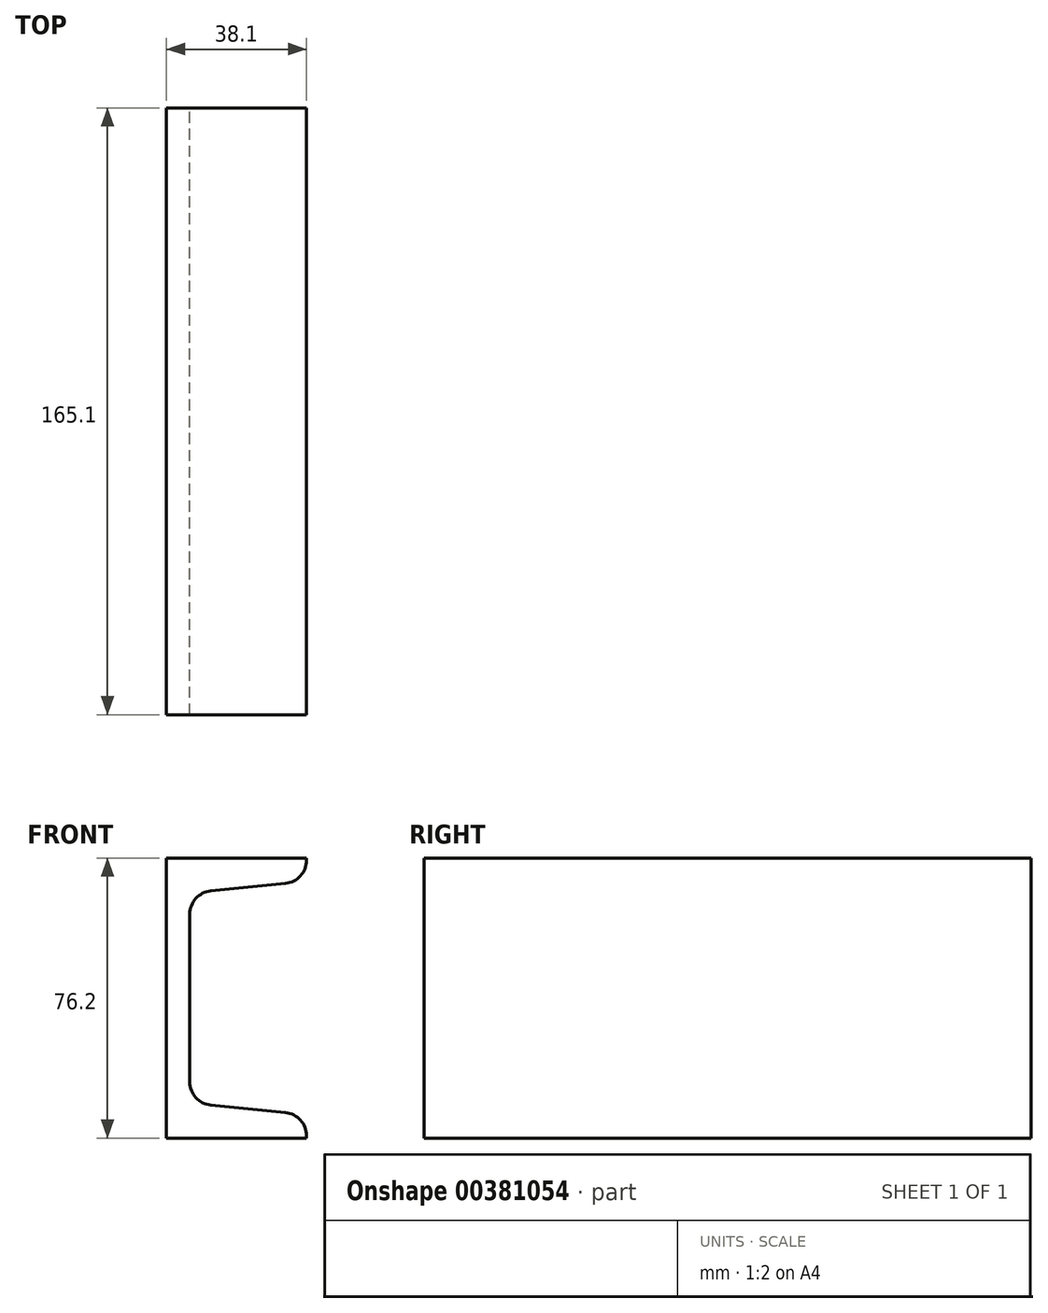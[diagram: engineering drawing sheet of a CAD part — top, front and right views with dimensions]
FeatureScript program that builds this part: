
annotation { "Feature Type Name" : "Feature", "Feature Type Description" : "" }
export const myFeature = defineFeature(function(context is Context, id is Id, definition is map)
    precondition{}
    {
        {
            var Q0;
            Q0=qCreatedBy(makeId("Front.planeOp"),FACE);
            var sketch = newSketch(context, id + "F0", { "sketchPlane" : qUnion([Q0])});
            skLineSegment(sketch, "E0", {"start": v(-3.27, 34.67) * mm, "end": v(-3.27, -41.53) * mm});
            skLineSegment(sketch, "E1", {"start": v(-3.27, 34.67) * mm, "end": v(34.83, 34.67) * mm});
            skLineSegment(sketch, "E2", {"start": v(34.83, -41.53) * mm, "end": v(34.83, -40.92) * mm});
            skLineSegment(sketch, "E3", {"start": v(29.11, -34.6) * mm, "end": v(8.8, -32.57) * mm});
            skLineSegment(sketch, "E4", {"start": v(3.08, -26.25) * mm, "end": v(3.08, 19.4) * mm});
            skLineSegment(sketch, "E5", {"start": v(8.8, 25.72) * mm, "end": v(29.11, 27.75) * mm});
            skLineSegment(sketch, "E6", {"start": v(34.83, 34.67) * mm, "end": v(34.83, 34.07) * mm});
            skLineSegment(sketch, "E7", {"start": v(-3.27, -41.53) * mm, "end": v(34.83, -41.53) * mm});
            skPoint(sketch, "E8.visualSharp", {"position": v(34.83, -35.18) * mm});
            skArc(sketch, "E8.filletArc", {"start": v(34.83, -40.92) * mm, "mid": v(33.19, -36.66) * mm, "end": v(29.11, -34.6) * mm});
            skPoint(sketch, "E9.visualSharp", {"position": v(34.83, 28.32) * mm});
            skArc(sketch, "E9.filletArc", {"start": v(29.11, 27.75) * mm, "mid": v(33.19, 29.8) * mm, "end": v(34.83, 34.07) * mm});
            skPoint(sketch, "E10.visualSharp", {"position": v(3.08, -32) * mm});
            skArc(sketch, "E10.filletArc", {"start": v(3.08, -26.25) * mm, "mid": v(4.72, -30.52) * mm, "end": v(8.8, -32.57) * mm});
            skPoint(sketch, "E11.visualSharp", {"position": v(3.08, 25.15) * mm});
            skArc(sketch, "E11.filletArc", {"start": v(8.8, 25.72) * mm, "mid": v(4.72, 23.66) * mm, "end": v(3.08, 19.4) * mm});
            skPoint(sketch, "E12", {"position": v(-0.1, -0.02) * mm});
            skSolve(sketch);
        }
        {
            var Q0;
            Q0=makeQuery(id+"F0.imprint","IMPRINT",FACE,{"disambiguationData":[TD([[makeQuery(id+"F0.imprint","IMPRINT",EDGE,{"derivedFrom":sQuery(id+"F0.wireOp",EDGE,"E0")}),1.0]])]});
            extrude(context, id + "F1", {"entities" : qUnion([Q0]), "depth" : 165.1 * mm, "symmetric" : true});
        }
    });
